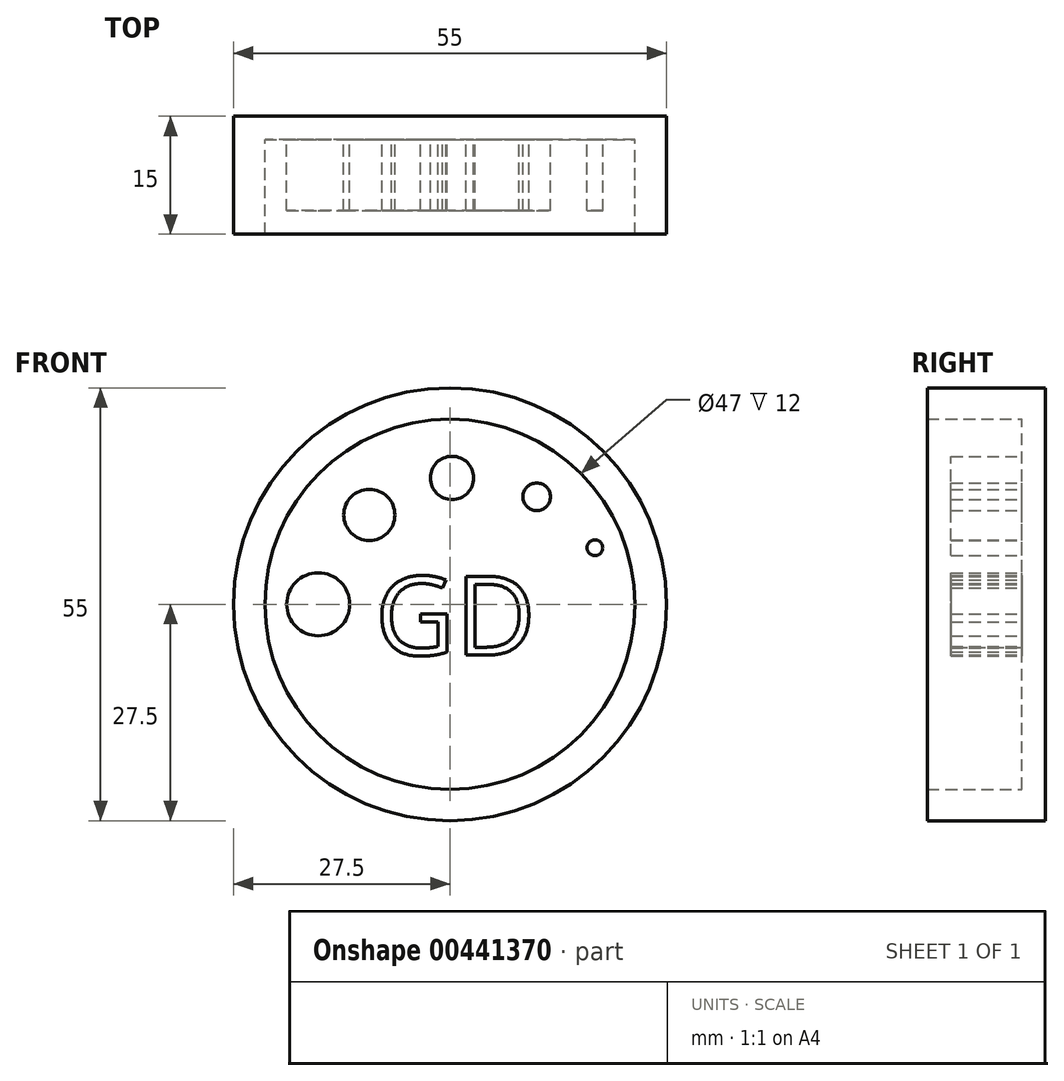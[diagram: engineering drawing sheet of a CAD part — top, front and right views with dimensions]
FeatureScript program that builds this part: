
annotation { "Feature Type Name" : "Feature", "Feature Type Description" : "" }
export const myFeature = defineFeature(function(context is Context, id is Id, definition is map)
    precondition{}
    {
        {
            var Q0;
            Q0=qCreatedBy(makeId("Front.planeOp"),FACE);
            var sketch = newSketch(context, id + "F0", { "sketchPlane" : qUnion([Q0])});
            skCircle(sketch, "E0", {"center": v(0, 0) * mm, "radius": 23.5 * mm});
            skCircle(sketch, "E1", {"center": v(0, 0) * mm, "radius": 27.5 * mm});
            skSolve(sketch);
        }
        {
            var Q0;
            Q0 = qSketchRegion(id + "F0", true);
            extrude(context, id + "F1", {"entities" : qUnion([Q0]), "depth" : 12 * mm});
        }
        {
            var Q0;
            Q0=qCreatedBy(makeId("Front.planeOp"),FACE);
            var sketch = newSketch(context, id + "F2", { "sketchPlane" : qUnion([Q0])});
            skCircle(sketch, "E2", {"center": v(0, 0) * mm, "radius": 27.5 * mm});
            skSolve(sketch);
        }
        {
            var Q0;
            Q0 = qSketchRegion(id + "F2", true);
            extrude(context, id + "F3", {"entities" : qUnion([Q0]), "operationType" : NewBodyOperationType.ADD, "oppositeDirection" : true, "depth" : 3 * mm});
        }
        {
            var Q0;
            Q0=qCreatedBy(makeId("Front.planeOp"),FACE);
            var sketch = newSketch(context, id + "F4", { "sketchPlane" : qUnion([Q0])});
            skCircle(sketch, "E3", {"center": v(-16.73, 0) * mm, "radius": 4 * mm});
            skCircle(sketch, "E4", {"center": v(-10.24, 11.35) * mm, "radius": 3.25 * mm});
            skCircle(sketch, "E5", {"center": v(0.26, 16.04) * mm, "radius": 2.75 * mm});
            skCircle(sketch, "E6", {"center": v(11.02, 13.65) * mm, "radius": 1.75 * mm});
            skCircle(sketch, "E7", {"center": v(18.41, 7.18) * mm, "radius": 1 * mm});
            skSolve(sketch);
        }
        {
            var Q0;
            Q0 = qSketchRegion(id + "F4", true);
            extrude(context, id + "F5", {"entities" : qUnion([Q0]), "operationType" : NewBodyOperationType.ADD, "depth" : 9 * mm});
        }
        {
            var Q0;
            Q0=qCreatedBy(makeId("Front.planeOp"),FACE);
            var sketch = newSketch(context, id + "F6", { "sketchPlane" : qUnion([Q0])});
            skText(sketch, "E8", { "text": "GD", "fontName": "OpenSans-Regular.ttf"});
            const initialGuessF6  = {"E8": [-0.00951, -0.00646, 1, 0, 0.01007]};
            skSetInitialGuess(sketch, initialGuessF6);
            skSolve(sketch);
        }
        {
            var Q0;
            Q0 = qSketchRegion(id + "F6", true);
            extrude(context, id + "F7", {"entities" : qUnion([Q0]), "operationType" : NewBodyOperationType.ADD, "depth" : 9 * mm});
        }
    });
